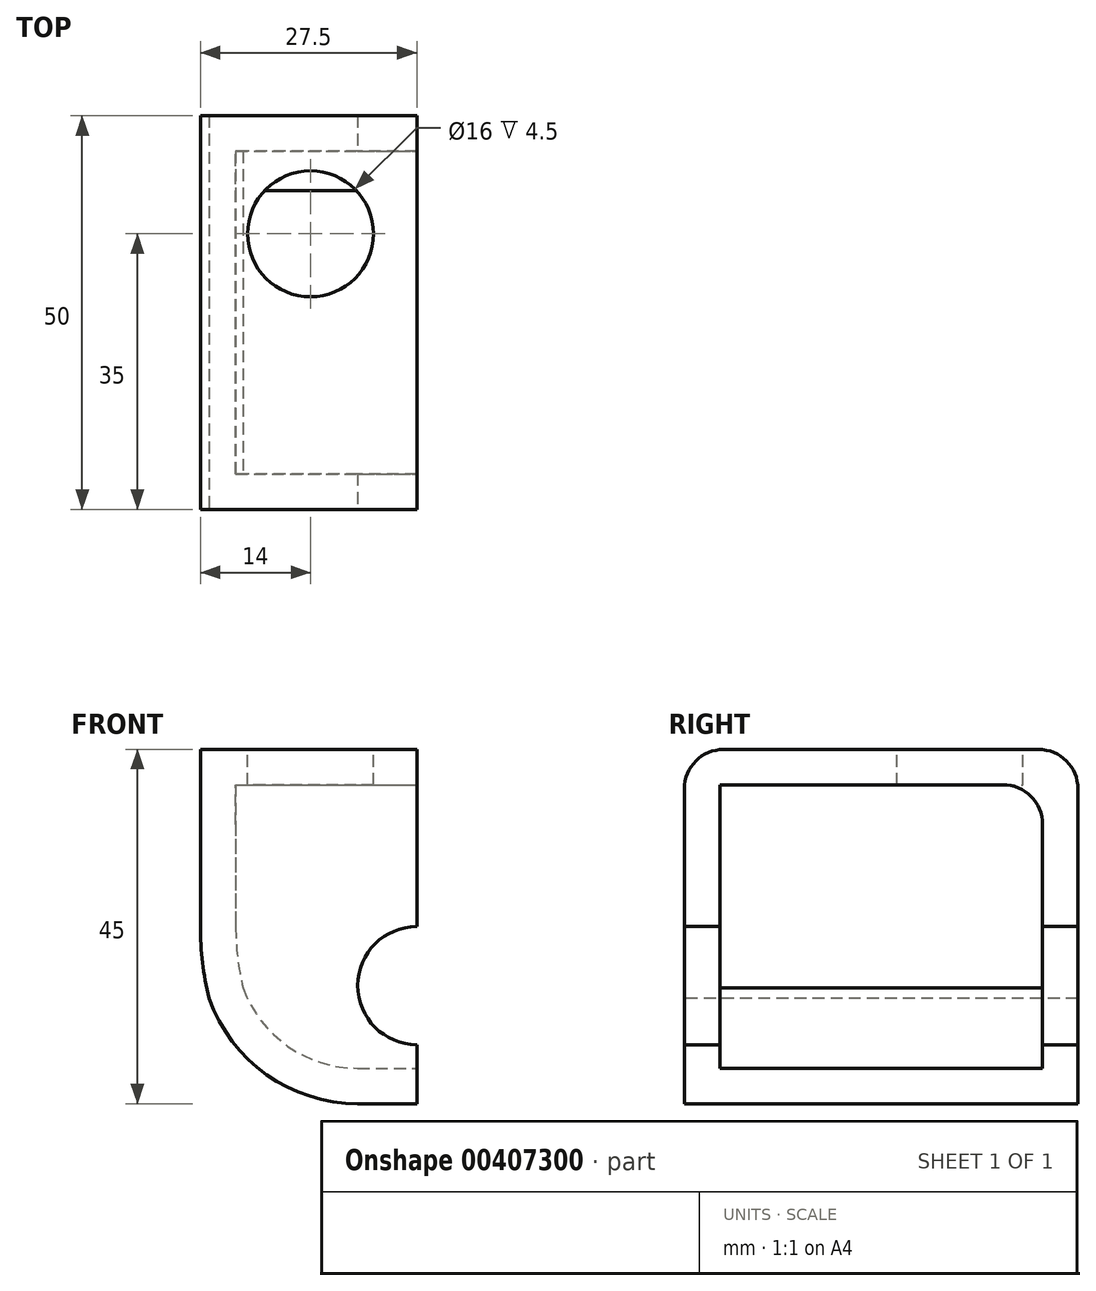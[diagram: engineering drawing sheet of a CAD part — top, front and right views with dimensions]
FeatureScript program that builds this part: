
annotation { "Feature Type Name" : "Feature", "Feature Type Description" : "" }
export const myFeature = defineFeature(function(context is Context, id is Id, definition is map)
    precondition{}
    {
        {
            var Q0;
            Q0=qCreatedBy(makeId("Top.planeOp"),FACE);
            var sketch = newSketch(context, id + "F0", { "sketchPlane" : qUnion([Q0])});
            skLineSegment(sketch, "E0.bottom", {"start": v(0, 0) * mm, "end": v(27.5, 0) * mm});
            skLineSegment(sketch, "E0.top", {"start": v(0, -50) * mm, "end": v(27.5, -50) * mm});
            skLineSegment(sketch, "E0.left", {"start": v(0, 0) * mm, "end": v(0, -50) * mm});
            skLineSegment(sketch, "E0.right", {"start": v(27.5, 0) * mm, "end": v(27.5, -50) * mm});
            skSolve(sketch);
        }
        {
            var Q0;
            Q0=makeQuery(id+"F0.imprint","IMPRINT",FACE,{"disambiguationData":[TD([[makeQuery(id+"F0.imprint","IMPRINT",EDGE,{"derivedFrom":sQuery(id+"F0.wireOp",EDGE,"E0.bottom")}),-1.0]])]});
            extrude(context, id + "F1", {"entities" : qUnion([Q0]), "depth" : 45 * mm});
        }
        {
            var Q0;
            Q0=makeQuery(id+"F1.opExtrude","SWEPT_FACE",FACE,{"disambiguationData":[OSD([sQuery(id+"F0.wireOp",EDGE,"E0.top")])]});
            var sketch = newSketch(context, id + "F2", { "sketchPlane" : qUnion([Q0])});
            skLineSegment(sketch, "E1", {"start": v(27.5, 0) * mm, "end": v(27.5, 15) * mm});
            skCircle(sketch, "E2", {"center": v(27.5, 15) * mm, "radius": 7.5 * mm});
            skLineSegment(sketch, "E3", {"start": v(27.5, 0) * mm, "end": v(7.5, 0) * mm});
            skLineSegment(sketch, "E4", {"start": v(7.5, 0) * mm, "end": v(7.5, 22.5) * mm});
            skPoint(sketch, "E4.endSnap0", {"position": v(27.5, 22.5) * mm});
            skLineSegment(sketch, "E5", {"start": v(7.5, 22.5) * mm, "end": v(0, 22.5) * mm});
            skLineSegment(sketch, "E6", {"start": v(0, 22.5) * mm, "end": v(0, 0) * mm});
            skLineSegment(sketch, "E7", {"start": v(0, 0) * mm, "end": v(7.5, 0) * mm});
            skArc(sketch, "E8", {"start": v(0, 22.5) * mm, "mid": v(1.92, 10.64) * mm, "end": v(7.5, 0) * mm});
            skSolve(sketch);
        }
        {
            var Q0;
            Q0=makeQuery(id+"F1.opExtrude","CAP_EDGE",EDGE,{"disambiguationData":[OSD([sQuery(id+"F0.wireOp",EDGE,"E0.left")])],"isStart":true});
            fillet(context, id + "F3", {"entities" : qUnion([Q0]), "radius" : 20 * mm, "tangentPropagation" : true, "allowEdgeOverflow" : false});
        }
        {
            var Q0;
            Q0=makeQuery(id+"F2.imprint","IMPRINT",FACE,{"disambiguationData":[TD([[makeQuery(id+"F2.imprint","IMPRINT",EDGE,{"derivedFrom":sQuery(id+"F2.wireOp",EDGE,"E6")}),1.0]])]});
            var Q1;
            {var subQ0=sQuery(id+"F2.wireOp",EDGE,"E1");var subQ3=sQuery(id+"F2.wireOp",EDGE,"E2");var subQ4=makeQuery(id+"F2.imprint","INTERSECT",VERTEX,{"derivedFrom":[subQ0,subQ3]});Q1=makeQuery(id+"F2.imprint","IMPRINT",FACE,{"disambiguationData":[TD([[makeQuery(id+"F2.imprint","IMPRINT",EDGE,{"disambiguationData":[TD([[subQ4,1.0]])],"derivedFrom":subQ0}),-1.0]])]});}
            extrude(context, id + "F4", {"entities" : qUnion([Q0, Q1]), "operationType" : NewBodyOperationType.REMOVE, "oppositeDirection" : true, "depth" : 50 * mm});
        }
        {
            var Q0;
            {var subQ0=sQuery(id+"F0.wireOp",EDGE,"E0.bottom");var subQ1=sQuery(id+"F0.wireOp",EDGE,"E0.right");var subQ2=sQuery(id+"F0.wireOp",EDGE,"E0.top");Q0=makeQuery(id+"F4.boolean.opBoolean","SPLIT",FACE,{"disambiguationData":[TD([makeQuery(id+"F1.opExtrude","CAP_FACE",FACE,{"disambiguationData":[OSD([subQ0,subQ2,sQuery(id+"F0.wireOp",EDGE,"E0.left"),subQ1])],"isStart":false})])],"derivedFrom":makeQuery(id+"F1.opExtrude","SWEPT_FACE",FACE,{"disambiguationData":[OSD([subQ1])]})});}
            var Q1;
            Q1=makeQuery(id+"F4.boolean.opBoolean","COPY",FACE,{"derivedFrom":makeQuery(id+"F4.opExtrude","SWEPT_FACE",FACE,{"disambiguationData":[OSD([sQuery(id+"F2.wireOp",EDGE,"E2")])]})});
            var Q2;
            {var subQ0=sQuery(id+"F0.wireOp",EDGE,"E0.bottom");var subQ1=sQuery(id+"F0.wireOp",EDGE,"E0.right");var subQ2=sQuery(id+"F0.wireOp",EDGE,"E0.top");Q2=makeQuery(id+"F4.boolean.opBoolean","SPLIT",FACE,{"disambiguationData":[TD([makeQuery(id+"F1.opExtrude","CAP_FACE",FACE,{"disambiguationData":[OSD([subQ0,subQ2,sQuery(id+"F0.wireOp",EDGE,"E0.left"),subQ1])],"isStart":true})])],"derivedFrom":makeQuery(id+"F1.opExtrude","SWEPT_FACE",FACE,{"disambiguationData":[OSD([subQ1])]})});}
            shell(context, id + "F5", {"entities" : qUnion([Q0, Q1, Q2]), "thickness" : 4.5 * mm});
        }
        {
            var Q0;
            Q0=makeQuery(id+"F1.opExtrude","CAP_EDGE",EDGE,{"disambiguationData":[OSD([sQuery(id+"F0.wireOp",EDGE,"E0.top")])],"isStart":false});
            var Q1;
            Q1=makeQuery(id+"F1.opExtrude","CAP_EDGE",EDGE,{"disambiguationData":[OSD([sQuery(id+"F0.wireOp",EDGE,"E0.bottom")])],"isStart":false});
            var Q2;
            {var subQ0=sQuery(id+"F0.wireOp",EDGE,"E0.bottom");Q2=makeQuery(id+"F5.opShell","OFFSET_EDGE",EDGE,{"disambiguationData":[OSD([subQ0]),TDD([makeQuery(id+"F1.opExtrude","CAP_EDGE",EDGE,{"disambiguationData":[OSD([subQ0])],"isStart":false})])]});}
            fillet(context, id + "F6", {"entities" : qUnion([Q0, Q1, Q2]), "radius" : 5 * mm, "tangentPropagation" : true, "allowEdgeOverflow" : false});
        }
        {
            var Q0;
            Q0=makeQuery(id+"F1.opExtrude","CAP_FACE",FACE,{"disambiguationData":[OSD([sQuery(id+"F0.wireOp",EDGE,"E0.bottom"),sQuery(id+"F0.wireOp",EDGE,"E0.top"),sQuery(id+"F0.wireOp",EDGE,"E0.left"),sQuery(id+"F0.wireOp",EDGE,"E0.right")])],"isStart":false});
            var sketch = newSketch(context, id + "F7", { "sketchPlane" : qUnion([Q0])});
            skLineSegment(sketch, "E9", {"start": v(0, 0) * mm, "end": v(27.5, 0) * mm});
            skLineSegment(sketch, "E10", {"start": v(27.5, 0) * mm, "end": v(14, 0) * mm});
            skLineSegment(sketch, "E11", {"start": v(14, 0) * mm, "end": v(14, -5) * mm});
            skLineSegment(sketch, "E12", {"start": v(14, -5) * mm, "end": v(14, -15) * mm});
            skCircle(sketch, "E13", {"center": v(14, -15) * mm, "radius": 8 * mm});
            skSolve(sketch);
        }
        {
            var Q0;
            Q0 = qSketchRegion(id + "F7", true);
            extrude(context, id + "F8", {"entities" : qUnion([Q0]), "operationType" : NewBodyOperationType.REMOVE, "oppositeDirection" : true, "depth" : 4.5 * mm});
        }
    });
